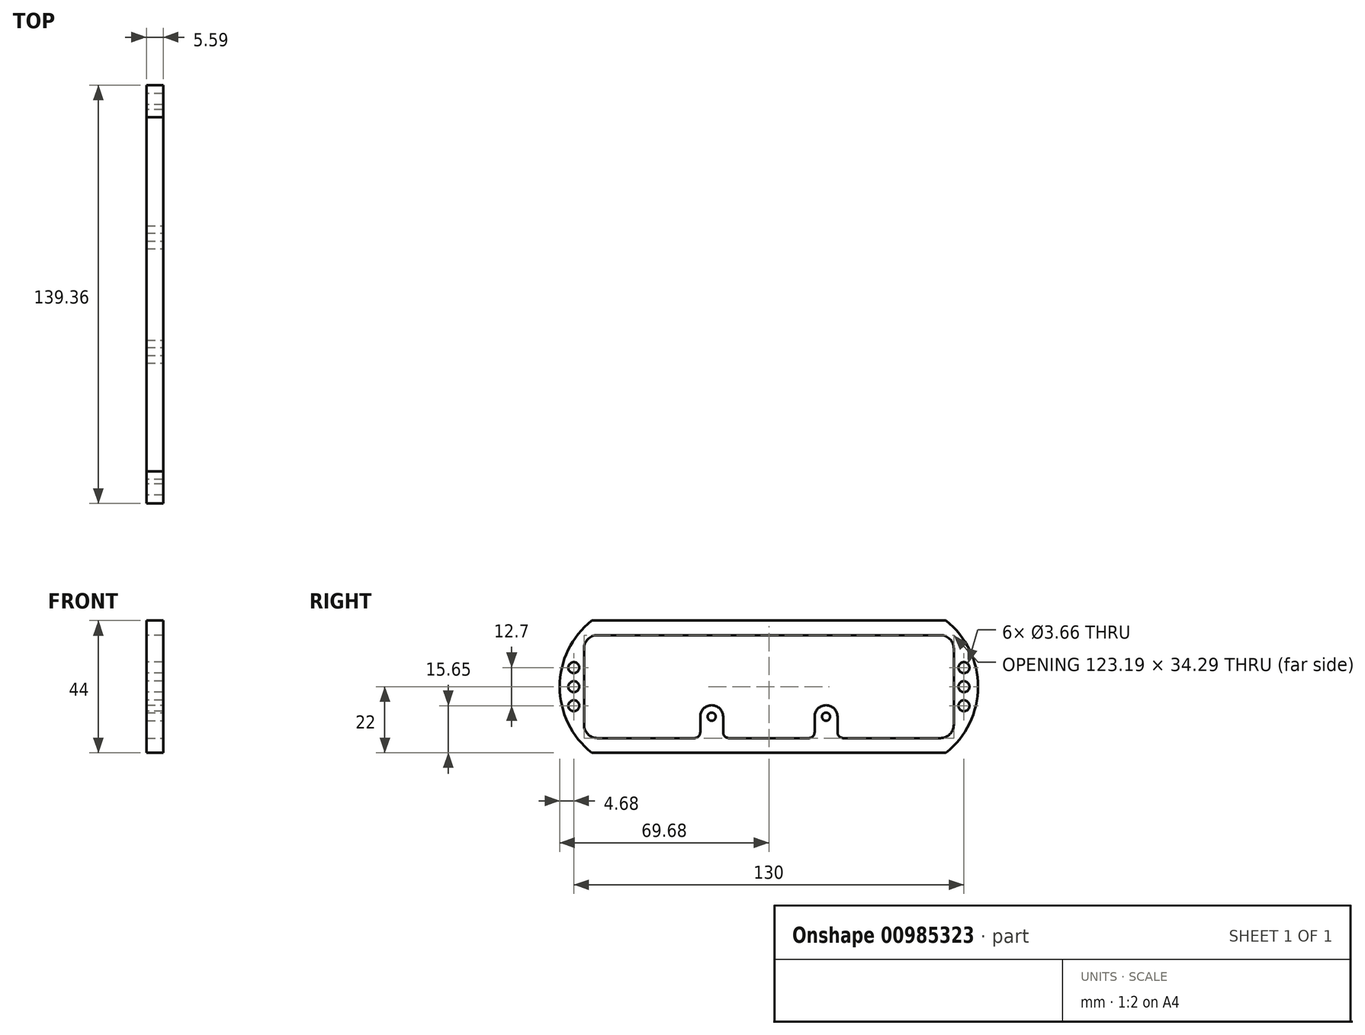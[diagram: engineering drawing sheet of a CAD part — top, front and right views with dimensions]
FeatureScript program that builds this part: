
annotation { "Feature Type Name" : "Feature", "Feature Type Description" : "" }
export const myFeature = defineFeature(function(context is Context, id is Id, definition is map)
    precondition{}
    {
        {
            var Q0;
            Q0=qCreatedBy(makeId("Right.planeOp"),FACE);
            var sketch = newSketch(context, id + "F0", { "sketchPlane" : qUnion([Q0])});
            skLineSegment(sketch, "E0.rect.bottom", {"start": v(59, 22) * mm, "end": v(-59, 22) * mm});
            skLineSegment(sketch, "E0.rect.top", {"start": v(59, -22) * mm, "end": v(-59, -22) * mm});
            skLineSegment(sketch, "E0.rect.left", {"start": v(59, 22) * mm, "end": v(59, -22) * mm, "construction": true});
            skLineSegment(sketch, "E0.rect.right", {"start": v(-59, 22) * mm, "end": v(-59, -22) * mm, "construction": true});
            skPoint(sketch, "E0.rect.middle", {"position": v(0, 0) * mm});
            skLineSegment(sketch, "E1", {"start": v(-59, 0) * mm, "end": v(59, 0) * mm, "construction": true});
            skArc(sketch, "E2", {"start": v(-59, 22) * mm, "mid": v(-69.68, 0) * mm, "end": v(-59, -22) * mm});
            skArc(sketch, "E3", {"start": v(59, -22) * mm, "mid": v(69.68, 0) * mm, "end": v(59, 22) * mm});
            skLineSegment(sketch, "E4.0", {"start": v(61.6, 17.14) * mm, "end": v(-61.6, 17.15) * mm});
            skLineSegment(sketch, "E4.2", {"start": v(61.6, -17.15) * mm, "end": v(-61.6, -17.14) * mm});
            skLineSegment(sketch, "E5.0", {"start": v(-61.6, 17.14) * mm, "end": v(-61.6, -17.14) * mm});
            skLineSegment(sketch, "E6.0", {"start": v(61.6, 17.15) * mm, "end": v(61.6, -17.15) * mm});
            skCircle(sketch, "E7", {"center": v(-65, 0) * mm, "radius": 1.83 * mm});
            skCircle(sketch, "E8", {"center": v(65, 0) * mm, "radius": 1.83 * mm});
            skLineSegment(sketch, "E9", {"start": v(-61.6, 17.14) * mm, "end": v(61.6, -17.15) * mm, "construction": true});
            skCircle(sketch, "E10", {"center": v(-65, 6.35) * mm, "radius": 1.83 * mm});
            skCircle(sketch, "E11", {"center": v(65, 6.35) * mm, "radius": 1.83 * mm});
            skCircle(sketch, "E12", {"center": v(65, -6.35) * mm, "radius": 1.83 * mm});
            skCircle(sketch, "E13", {"center": v(-65, -6.35) * mm, "radius": 1.83 * mm});
            skLineSegment(sketch, "E14", {"start": v(-65, 6.35) * mm, "end": v(-65, -6.35) * mm, "construction": true});
            skSolve(sketch);
        }
        {
            var Q0;
            Q0=makeQuery(id+"F0.imprint","IMPRINT",FACE,{"disambiguationData":[TD([[makeQuery(id+"F0.imprint","IMPRINT",EDGE,{"derivedFrom":sQuery(id+"F0.wireOp",EDGE,"E0.rect.bottom")}),1.0]])]});
            extrude(context, id + "F1", {"entities" : qUnion([Q0]), "depth" : 5.6 * mm});
        }
        {
            var Q0;
            Q0=makeQuery(id+"F1.opExtrude","SWEPT_EDGE",EDGE,{"disambiguationData":[OSD([sQuery(id+"F0.wireOp",EDGE,"E4.0"),sQuery(id+"F0.wireOp",EDGE,"E5.0")])]});
            var Q1;
            Q1=makeQuery(id+"F1.opExtrude","SWEPT_EDGE",EDGE,{"disambiguationData":[OSD([sQuery(id+"F0.wireOp",EDGE,"E4.2"),sQuery(id+"F0.wireOp",EDGE,"E5.0")])]});
            var Q2;
            Q2=makeQuery(id+"F1.opExtrude","SWEPT_EDGE",EDGE,{"disambiguationData":[OSD([sQuery(id+"F0.wireOp",EDGE,"E4.2"),sQuery(id+"F0.wireOp",EDGE,"E6.0")])]});
            var Q3;
            Q3=makeQuery(id+"F1.opExtrude","SWEPT_EDGE",EDGE,{"disambiguationData":[OSD([sQuery(id+"F0.wireOp",EDGE,"E4.0"),sQuery(id+"F0.wireOp",EDGE,"E6.0")])]});
            fillet(context, id + "F2", {"entities" : qUnion([Q0, Q1, Q2, Q3]), "radius" : 4.44 * mm, "tangentPropagation" : true, "allowEdgeOverflow" : false});
        }
        {
            var Q0;
            Q0=makeQuery(id+"F1.opExtrude","CAP_FACE",FACE,{"disambiguationData":[OSD([sQuery(id+"F0.wireOp",EDGE,"E0.rect.bottom"),sQuery(id+"F0.wireOp",EDGE,"E0.rect.top"),sQuery(id+"F0.wireOp",EDGE,"E2"),sQuery(id+"F0.wireOp",EDGE,"E3"),sQuery(id+"F0.wireOp",EDGE,"E4.0"),sQuery(id+"F0.wireOp",EDGE,"E4.2"),sQuery(id+"F0.wireOp",EDGE,"E5.0"),sQuery(id+"F0.wireOp",EDGE,"E6.0"),sQuery(id+"F0.wireOp",EDGE,"E7"),sQuery(id+"F0.wireOp",EDGE,"E8"),sQuery(id+"F0.wireOp",EDGE,"E10"),sQuery(id+"F0.wireOp",EDGE,"E11"),sQuery(id+"F0.wireOp",EDGE,"E12"),sQuery(id+"F0.wireOp",EDGE,"E13")])],"isStart":false});
            var sketch = newSketch(context, id + "F3", { "sketchPlane" : qUnion([Q0])});
            skCircle(sketch, "E15", {"center": v(-19.05, -10) * mm, "radius": 1.35 * mm});
            skArc(sketch, "E16", {"start": v(-15.24, -10) * mm, "mid": v(-19.05, -6.19) * mm, "end": v(-22.86, -10) * mm});
            skLineSegment(sketch, "E17", {"start": v(-22.86, -10) * mm, "end": v(-22.86, -15.15) * mm});
            skLineSegment(sketch, "E18", {"start": v(-15.24, -10) * mm, "end": v(-15.24, -15.15) * mm});
            skArc(sketch, "E19.filletArc", {"start": v(-24.86, -17.15) * mm, "mid": v(-23.45, -16.56) * mm, "end": v(-22.86, -15.15) * mm});
            skArc(sketch, "E20.filletArc", {"start": v(-15.24, -15.15) * mm, "mid": v(-14.65, -16.56) * mm, "end": v(-13.24, -17.15) * mm});
            skLineSegment(sketch, "E21", {"start": v(-24.86, -17.15) * mm, "end": v(-13.24, -17.15) * mm});
            skLineSegment(sketch, "E22.1.0.0", {"start": v(22.86, -10) * mm, "end": v(22.86, -15.15) * mm});
            skLineSegment(sketch, "E22.1.0.1", {"start": v(13.24, -17.15) * mm, "end": v(24.86, -17.15) * mm});
            skArc(sketch, "E22.1.0.3", {"start": v(22.86, -10) * mm, "mid": v(19.05, -6.19) * mm, "end": v(15.24, -10) * mm});
            skLineSegment(sketch, "E22.1.0.4", {"start": v(15.24, -10) * mm, "end": v(15.24, -15.15) * mm});
            skCircle(sketch, "E22.1.0.5", {"center": v(19.05, -10) * mm, "radius": 1.35 * mm});
            skArc(sketch, "E22.1.0.6", {"start": v(22.86, -15.15) * mm, "mid": v(23.45, -16.56) * mm, "end": v(24.86, -17.15) * mm});
            skArc(sketch, "E22.1.0.7", {"start": v(13.24, -17.15) * mm, "mid": v(14.65, -16.56) * mm, "end": v(15.24, -15.15) * mm});
            skLineSegment(sketch, "E22.direction1", {"start": v(-13.24, -17.15) * mm, "end": v(13.24, -17.15) * mm, "construction": true});
            skLineSegment(sketch, "E23", {"start": v(0, -17.15) * mm, "end": v(0, 0) * mm, "construction": true});
            skSolve(sketch);
        }
        {
            var Q0;
            Q0=qSketchRegion(id+"F3",true);
            var Q1;
            Q1=makeQuery(id+"F1.opExtrude","CAP_FACE",FACE,{"disambiguationData":[OSD([sQuery(id+"F0.wireOp",EDGE,"E0.rect.bottom"),sQuery(id+"F0.wireOp",EDGE,"E0.rect.top"),sQuery(id+"F0.wireOp",EDGE,"E2"),sQuery(id+"F0.wireOp",EDGE,"E3"),sQuery(id+"F0.wireOp",EDGE,"E4.0"),sQuery(id+"F0.wireOp",EDGE,"E4.2"),sQuery(id+"F0.wireOp",EDGE,"E5.0"),sQuery(id+"F0.wireOp",EDGE,"E6.0"),sQuery(id+"F0.wireOp",EDGE,"E7"),sQuery(id+"F0.wireOp",EDGE,"E8"),sQuery(id+"F0.wireOp",EDGE,"E10"),sQuery(id+"F0.wireOp",EDGE,"E11"),sQuery(id+"F0.wireOp",EDGE,"E12"),sQuery(id+"F0.wireOp",EDGE,"E13")])],"isStart":true});
            extrude(context, id + "F4", {"entities" : qUnion([Q0]), "operationType" : NewBodyOperationType.ADD, "endBound" : BoundingType.UP_TO_SURFACE, "oppositeDirection" : true, "endBoundEntityFace" : qUnion([Q1]), "depth" : 25 * mm});
        }
    });
